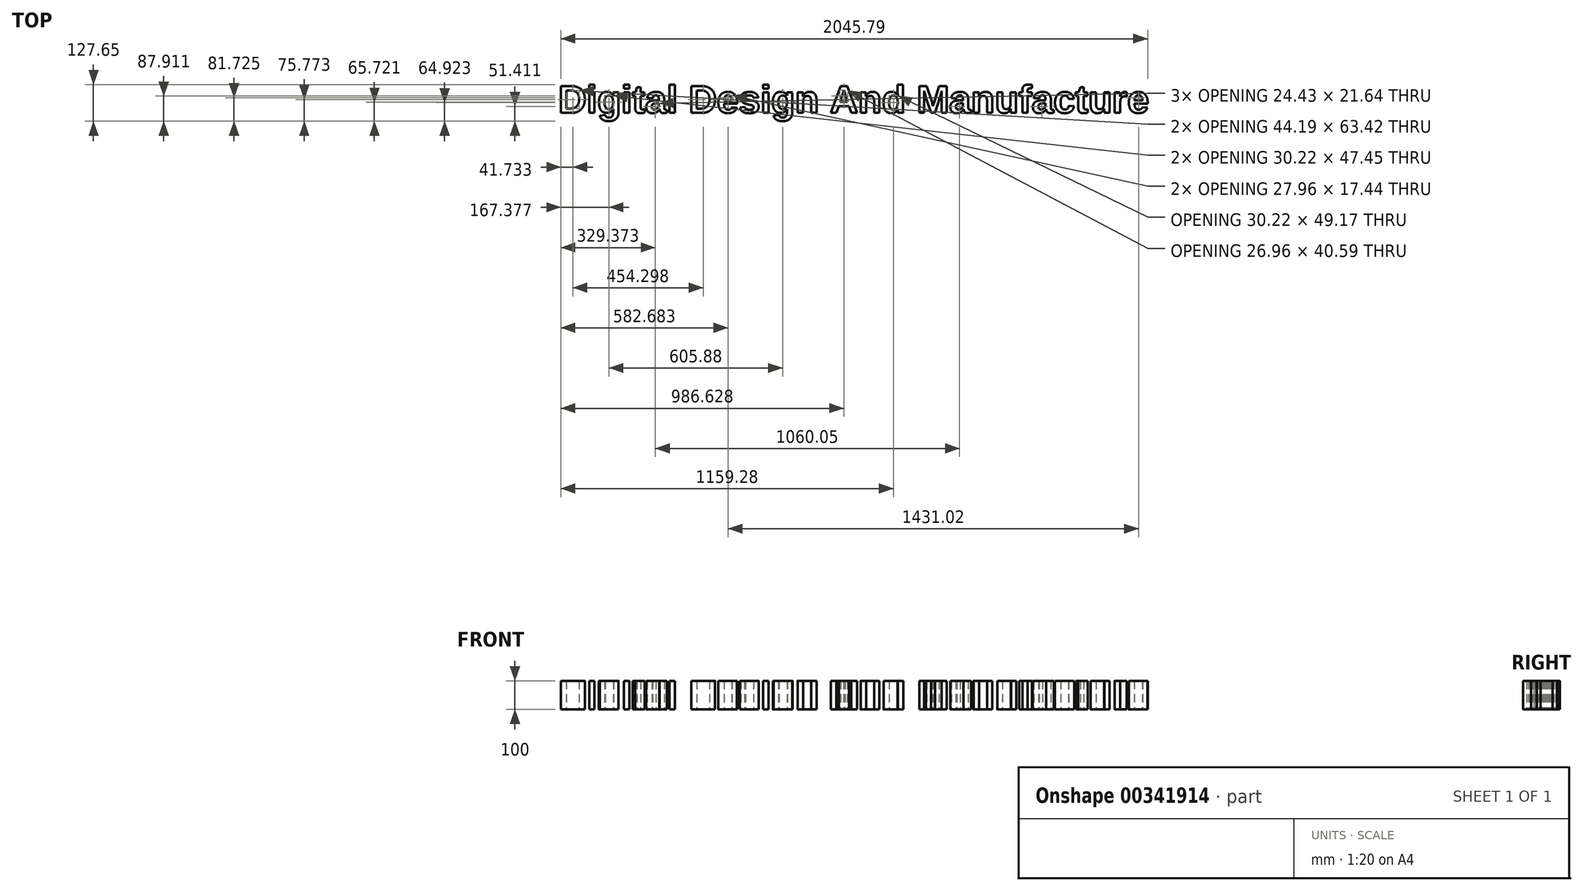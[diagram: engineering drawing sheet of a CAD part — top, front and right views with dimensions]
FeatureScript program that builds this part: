
annotation { "Feature Type Name" : "Feature", "Feature Type Description" : "" }
export const myFeature = defineFeature(function(context is Context, id is Id, definition is map)
    precondition{}
    {
        {
            var Q0;
            Q0=qCreatedBy(makeId("Top.planeOp"),FACE);
            var sketch = newSketch(context, id + "F0", { "sketchPlane" : qUnion([Q0])});
            skText(sketch, "E0", { "text": "Digital Design And Manufacture", "fontName": "Arimo-Bold.ttf"});
            const initialGuessF0  = {"E0": [-0.14323, 0.01184, 1, 0, 0.09813]};
            skSetInitialGuess(sketch, initialGuessF0);
            skSolve(sketch);
        }
        {
            var Q0;
            Q0 = qSketchRegion(id + "F0", true);
            extrude(context, id + "F1", {"entities" : qUnion([Q0]), "depth" : 100 * mm});
        }
        {
            var Q0;
            Q0=qCreatedBy(makeId("Front.planeOp"),FACE);
            var sketch = newSketch(context, id + "F2", { "sketchPlane" : qUnion([Q0])});
            skFitSpline(sketch, "E1", {"points": [v(-143.26, 64.6) * mm, v(1904.52, 59.97) * mm, v(1937.47, 64.57) * mm], "startDerivative": vector(3091.44, -208.45) * mm, "endDerivative": vector(17.55, 54.61) * mm});
            skSolve(sketch);
        }
        {
            var Q0;
            Q0=sQuery(id+"F2.wireOp",EDGE,"E1");
            extrude(context, id + "F3", {"bodyType" : ToolBodyType.SURFACE, "surfaceEntities" : qUnion([Q0]), "endBound" : BoundingType.SYMMETRIC, "oppositeDirection" : true, "depth" : 300 * mm});
        }
    });
